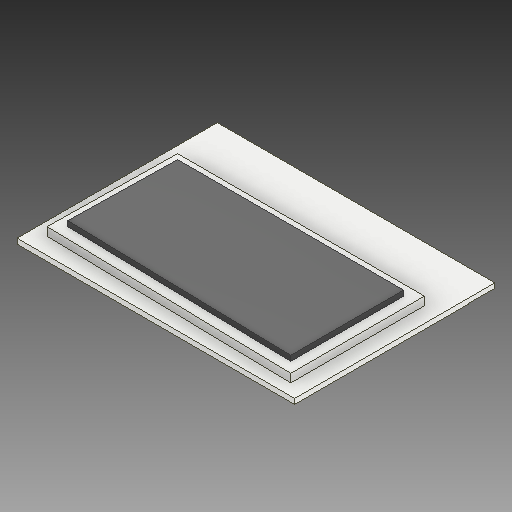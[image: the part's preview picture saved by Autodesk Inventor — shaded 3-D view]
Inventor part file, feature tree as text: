
AUTODESK INVENTOR PART (.ipt)
format: ipt  version: 2020 (Build 240168000, 168)  size: 261,120 bytes
history: native  units: mm
features: other x7, extrude x1, sketch x1
ambient origin geometry x8: Origin, YZ Plane, XZ Plane, XY Plane, X Axis, Y Axis, Z Axis, Center Point
bodies: Body1 (feature_tree), Body2 (feature_tree), Body3 (feature_tree), Body4 (feature_tree)
feature tree (9):
  other  "Твердое тело1"
  extrude  "Выдавливание1"  Depth=0.1mm TaperAngle=0.0deg
  other  "Твердое тело2"
  other  "Твердое тело3"
  sketch  "Эскиз2"
  other  "Твердое тело4"
  other  "pad"
  other  "glass1"
  other  "glass2"
